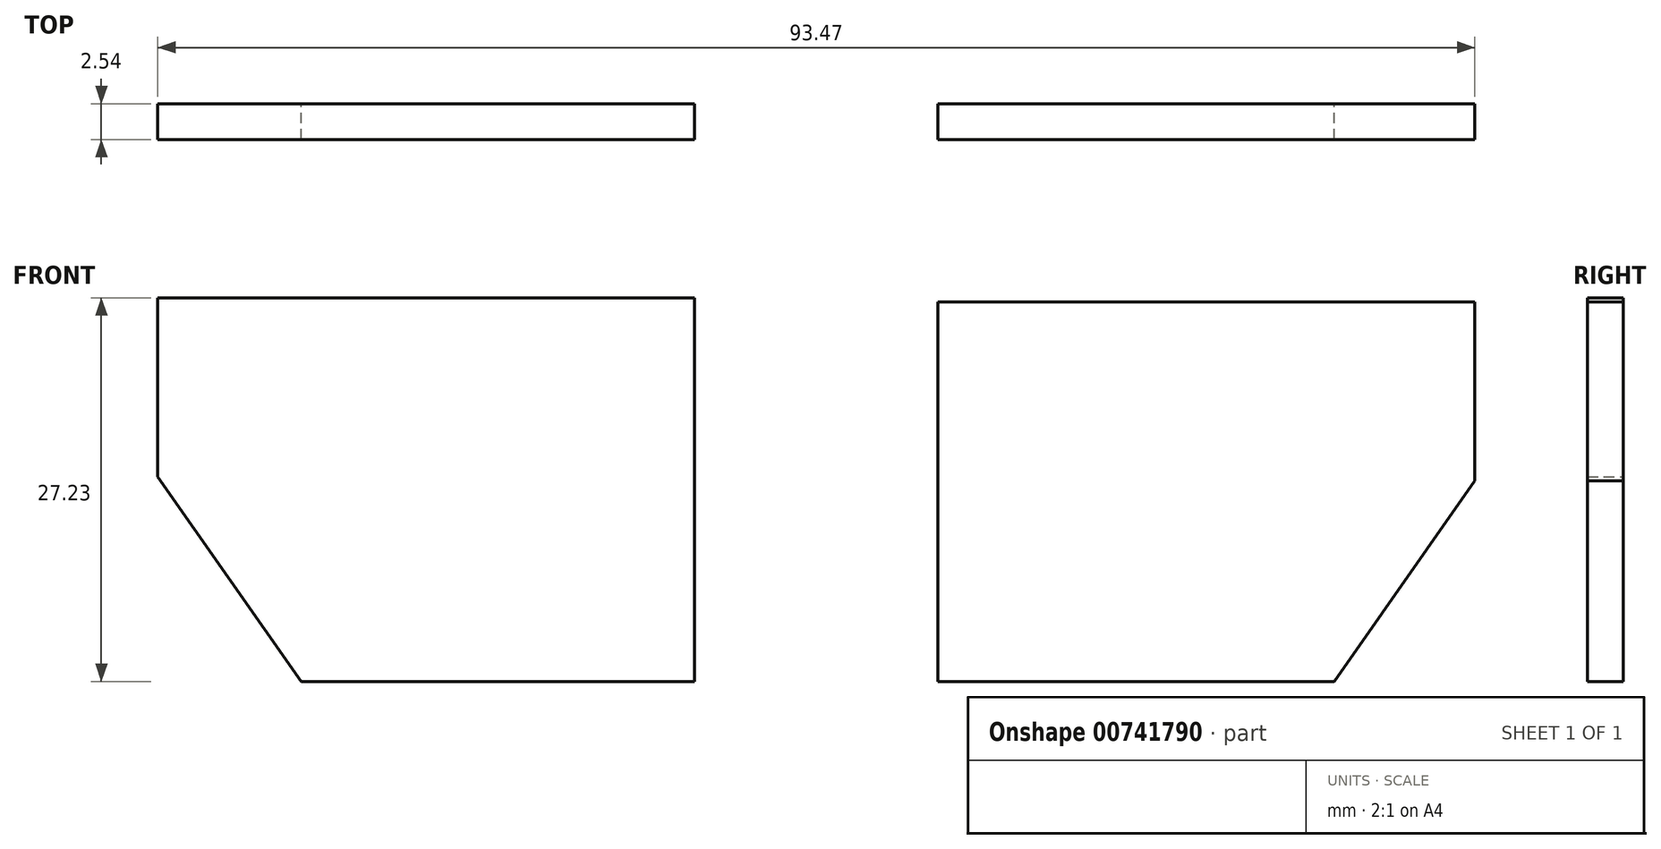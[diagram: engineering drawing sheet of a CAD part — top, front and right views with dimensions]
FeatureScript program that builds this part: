
annotation { "Feature Type Name" : "Feature", "Feature Type Description" : "" }
export const myFeature = defineFeature(function(context is Context, id is Id, definition is map)
    precondition{}
    {
        {
            var Q0;
            Q0=qCreatedBy(makeId("Front.planeOp"),FACE);
            var sketch = newSketch(context, id + "F0", { "sketchPlane" : qUnion([Q0])});
            skLineSegment(sketch, "E0.bottom", {"start": v(-41.24, -16.65) * mm, "end": v(-3.14, -16.65) * mm});
            skLineSegment(sketch, "E0.top", {"start": v(-41.24, 21.45) * mm, "end": v(-3.14, 21.45) * mm});
            skLineSegment(sketch, "E0.left", {"start": v(-41.24, -16.65) * mm, "end": v(-41.24, 21.45) * mm});
            skLineSegment(sketch, "E0.right", {"start": v(-3.14, -16.65) * mm, "end": v(-3.14, 21.45) * mm});
            skLineSegment(sketch, "E1.bottom", {"start": v(14.13, -16.93) * mm, "end": v(52.23, -16.93) * mm});
            skLineSegment(sketch, "E1.top", {"start": v(14.13, 21.17) * mm, "end": v(52.23, 21.17) * mm});
            skLineSegment(sketch, "E1.left", {"start": v(14.13, -16.93) * mm, "end": v(14.13, 21.17) * mm});
            skLineSegment(sketch, "E1.right", {"start": v(52.23, -16.93) * mm, "end": v(52.23, 21.17) * mm});
            skLineSegment(sketch, "E2", {"start": v(-41.24, 8.75) * mm, "end": v(-23.46, -16.65) * mm});
            skLineSegment(sketch, "E3", {"start": v(34.45, -16.93) * mm, "end": v(52.23, 8.47) * mm});
            skLineSegment(sketch, "E4", {"start": v(-41.24, -5.78) * mm, "end": v(52.23, -5.78) * mm});
            skSolve(sketch);
        }
        {
            var Q0;
            {var subQ2=sQuery(id+"F0.wireOp",EDGE,"E0.top");Q0=makeQuery(id+"F0.imprint","IMPRINT",FACE,{"disambiguationData":[TD([[makeQuery(id+"F0.imprint","IMPRINT",EDGE,{"derivedFrom":subQ2}),-1.0]])]});}
            var Q1;
            {var subQ1=sQuery(id+"F0.wireOp",EDGE,"E1.top");Q1=makeQuery(id+"F0.imprint","IMPRINT",FACE,{"disambiguationData":[TD([[makeQuery(id+"F0.imprint","IMPRINT",EDGE,{"derivedFrom":subQ1}),-1.0]])]});}
            extrude(context, id + "F1", {"entities" : qUnion([Q0, Q1]), "depth" : 2.54 * mm, "offsetDistance" : 25.4 * mm});
        }
    });
